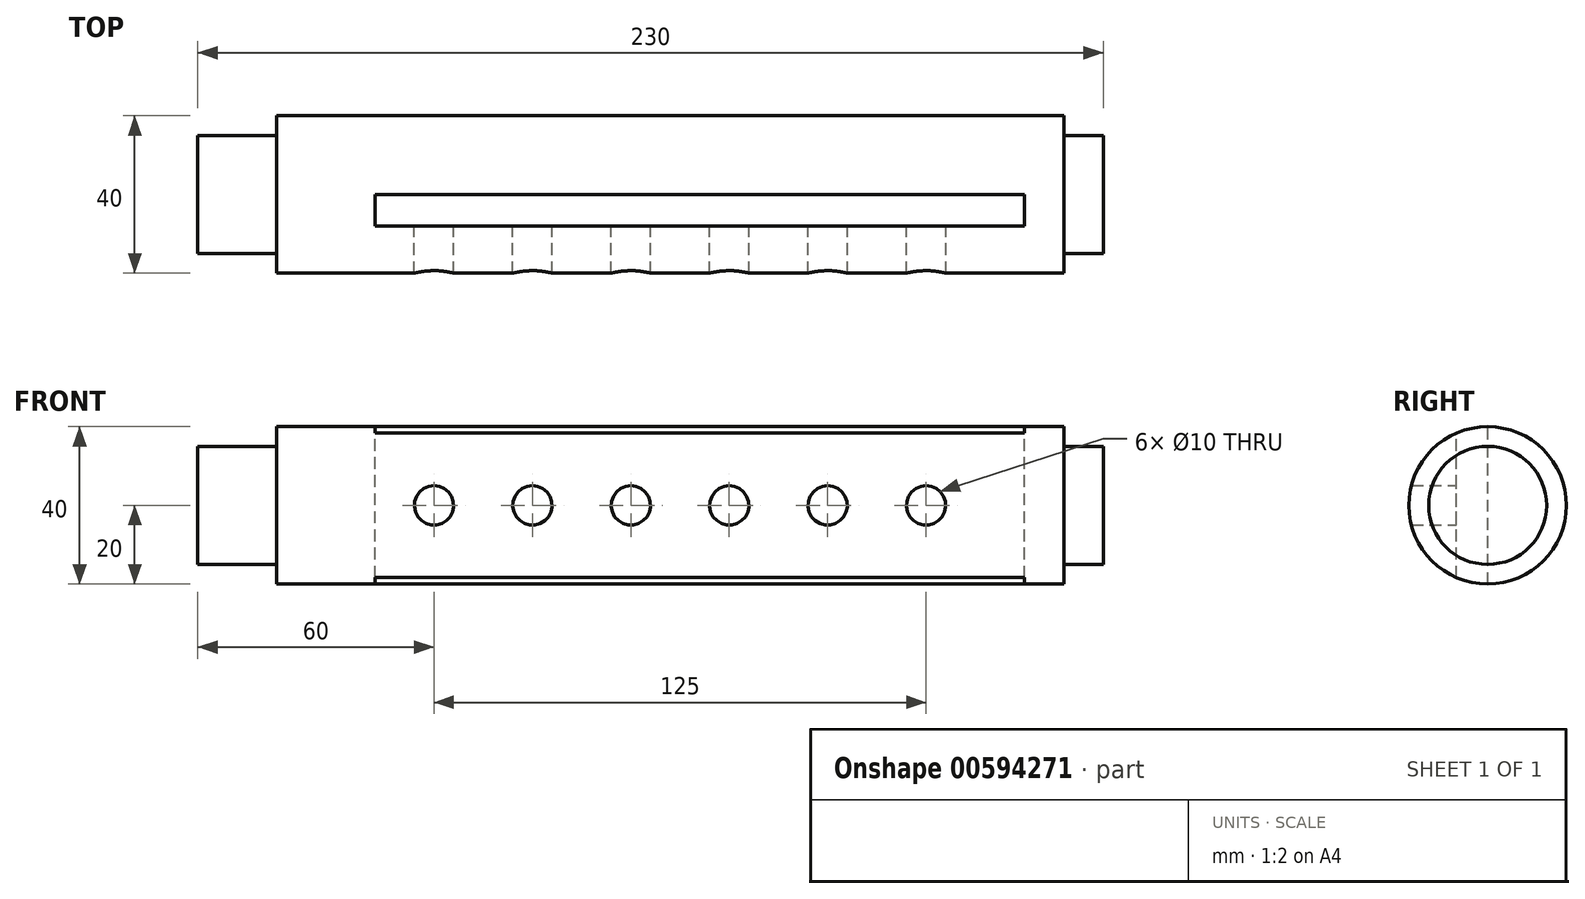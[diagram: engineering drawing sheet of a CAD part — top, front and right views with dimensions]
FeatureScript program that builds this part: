
annotation { "Feature Type Name" : "Feature", "Feature Type Description" : "" }
export const myFeature = defineFeature(function(context is Context, id is Id, definition is map)
    precondition{}
    {
        {
            var Q0;
            Q0=qCreatedBy(makeId("Right.planeOp"),FACE);
            var sketch = newSketch(context, id + "F0", { "sketchPlane" : qUnion([Q0])});
            skCircle(sketch, "E0", {"center": v(0, 0) * mm, "radius": 15 * mm});
            skSolve(sketch);
        }
        {
            var Q0;
            Q0=makeQuery(id+"F0.imprint","IMPRINT",FACE,{"disambiguationData":[TD([[makeQuery(id+"F0.imprint","IMPRINT",EDGE,{"derivedFrom":sQuery(id+"F0.wireOp",EDGE,"E0")}),1.0]])]});
            extrude(context, id + "F1", {"entities" : qUnion([Q0]), "depth" : 20 * mm, "offsetDistance" : 25 * mm});
        }
        {
            var Q0;
            Q0=makeQuery(id+"F1.opExtrude","CAP_FACE",FACE,{"disambiguationData":[OSD([sQuery(id+"F0.wireOp",EDGE,"E0")])],"isStart":false});
            var sketch = newSketch(context, id + "F2", { "sketchPlane" : qUnion([Q0])});
            skCircle(sketch, "E1", {"center": v(0, 0) * mm, "radius": 20 * mm});
            skSolve(sketch);
        }
        {
            var Q0;
            Q0 = qSketchRegion(id + "F2", true);
            extrude(context, id + "F3", {"entities" : qUnion([Q0]), "operationType" : NewBodyOperationType.ADD, "depth" : 200 * mm, "offsetDistance" : 25 * mm});
        }
        {
            var Q0;
            Q0=qCreatedBy(makeId("Top.planeOp"),FACE);
            var sketch = newSketch(context, id + "F4", { "sketchPlane" : qUnion([Q0])});
            skLineSegment(sketch, "E2.bottom", {"start": v(45, 0) * mm, "end": v(210, 0) * mm});
            skLineSegment(sketch, "E2.top", {"start": v(45, -8) * mm, "end": v(210, -8) * mm});
            skLineSegment(sketch, "E2.left", {"start": v(45, 0) * mm, "end": v(45, -8) * mm});
            skLineSegment(sketch, "E2.right", {"start": v(210, 0) * mm, "end": v(210, -8) * mm});
            skSolve(sketch);
        }
        {
            var Q0;
            Q0 = qSketchRegion(id + "F4", true);
            extrude(context, id + "F5", {"entities" : qUnion([Q0]), "operationType" : NewBodyOperationType.REMOVE, "endBound" : BoundingType.SYMMETRIC, "oppositeDirection" : true, "depth" : 50 * mm, "offsetDistance" : 25 * mm});
        }
        {
            var Q0;
            Q0=qCreatedBy(makeId("Front.planeOp"),FACE);
            var sketch = newSketch(context, id + "F6", { "sketchPlane" : qUnion([Q0])});
            skPoint(sketch, "E3", {"position": v(60, 0) * mm});
            skPoint(sketch, "E4", {"position": v(85, 0) * mm});
            skPoint(sketch, "E5", {"position": v(110, 0) * mm});
            skPoint(sketch, "E6", {"position": v(135, 0) * mm});
            skPoint(sketch, "E7", {"position": v(160, 0) * mm});
            skPoint(sketch, "E8", {"position": v(185, 0) * mm});
            skSolve(sketch);
        }
        {
            var Q0;
            Q0=sQuery(id+"F6.wireOp",VERTEX,"E3");
            var Q1;
            Q1=sQuery(id+"F6.wireOp",VERTEX,"E4");
            var Q2;
            Q2=sQuery(id+"F6.wireOp",VERTEX,"E5");
            var Q3;
            Q3=sQuery(id+"F6.wireOp",VERTEX,"E6");
            var Q4;
            Q4=sQuery(id+"F6.wireOp",VERTEX,"E7");
            var Q5;
            Q5=sQuery(id+"F6.wireOp",VERTEX,"E8");
            var Q6;
            Q6=makeQuery(id+"F1.opExtrude","SWEPT_BODY",BODY,{"disambiguationData":[OSD([sQuery(id+"F0.wireOp",EDGE,"E0")])]});
            hole(context, id + "F7", {"style" : HoleStyle.SIMPLE, "endStyle" : HoleEndStyle.THROUGH, "oppositeDirection" : true, "holeDiameter" : 10 * mm, "majorDiameter" : 5 * mm, "isTappedThrough" : true, "tappedDepth" : 12 * mm, "tapClearance" : 3, "locations" : qUnion([Q0, Q1, Q2, Q3, Q4, Q5]), "scope" : qUnion([Q6])});
        }
        {
            var Q0;
            {var subQ0=sQuery(id+"F2.wireOp",EDGE,"E1");Q0=makeQuery(id+"F5.boolean.opBoolean","SPLIT",FACE,{"disambiguationData":[TD([makeQuery(id+"F5.opExtrude","SWEPT_FACE",FACE,{"disambiguationData":[OSD([sQuery(id+"F4.wireOp",EDGE,"E2.bottom")])]})])],"derivedFrom":makeQuery(id+"F3.opExtrude","CAP_FACE",FACE,{"disambiguationData":[OSD([subQ0])],"isStart":false})});}
            var sketch = newSketch(context, id + "F8", { "sketchPlane" : qUnion([Q0])});
            skCircle(sketch, "E9", {"center": v(0, 0) * mm, "radius": 15 * mm});
            skSolve(sketch);
        }
        {
            var Q0;
            Q0=makeQuery(id+"F8.imprint","IMPRINT",FACE,{"disambiguationData":[TD([[makeQuery(id+"F8.imprint","IMPRINT",EDGE,{"derivedFrom":sQuery(id+"F8.wireOp",EDGE,"E9")}),1.0]])]});
            extrude(context, id + "F9", {"entities" : qUnion([Q0]), "operationType" : NewBodyOperationType.ADD, "depth" : 10 * mm, "offsetDistance" : 25 * mm});
        }
    });
